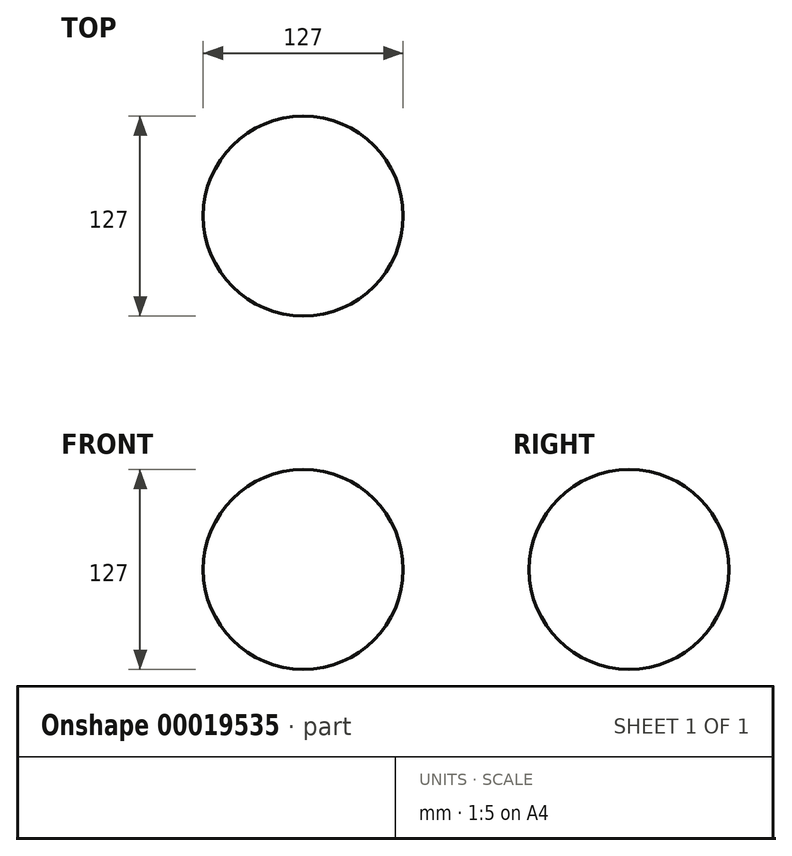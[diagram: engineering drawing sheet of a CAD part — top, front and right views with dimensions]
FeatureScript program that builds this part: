
annotation { "Feature Type Name" : "Feature", "Feature Type Description" : "" }
export const myFeature = defineFeature(function(context is Context, id is Id, definition is map)
    precondition{}
    {
        {
            var Q0;
            Q0=qCreatedBy(makeId("Front.planeOp"),FACE);
            var sketch = newSketch(context, id + "F0", { "sketchPlane" : qUnion([Q0])});
            skLineSegment(sketch, "E0", {"start": v(-63.5, 0) * mm, "end": v(63.5, 0) * mm});
            skArc(sketch, "E1", {"start": v(63.5, 0) * mm, "mid": v(0, 63.5) * mm, "end": v(-63.5, 0) * mm});
            skSolve(sketch);
        }
        {
            var Q0;
            Q0=makeQuery(id+"F0.imprint","IMPRINT",FACE,{"disambiguationData":[TD([[makeQuery(id+"F0.imprint","IMPRINT",EDGE,{"derivedFrom":sQuery(id+"F0.wireOp",EDGE,"E0")}),1.0]])]});
            var Q1;
            Q1=sQuery(id+"F0.wireOp",EDGE,"E0");
            revolve(context, id + "F1", {"entities" : qUnion([Q0]), "axis" : qUnion([Q1]), "revolveType" : RevolveType.FULL});
        }
    });
